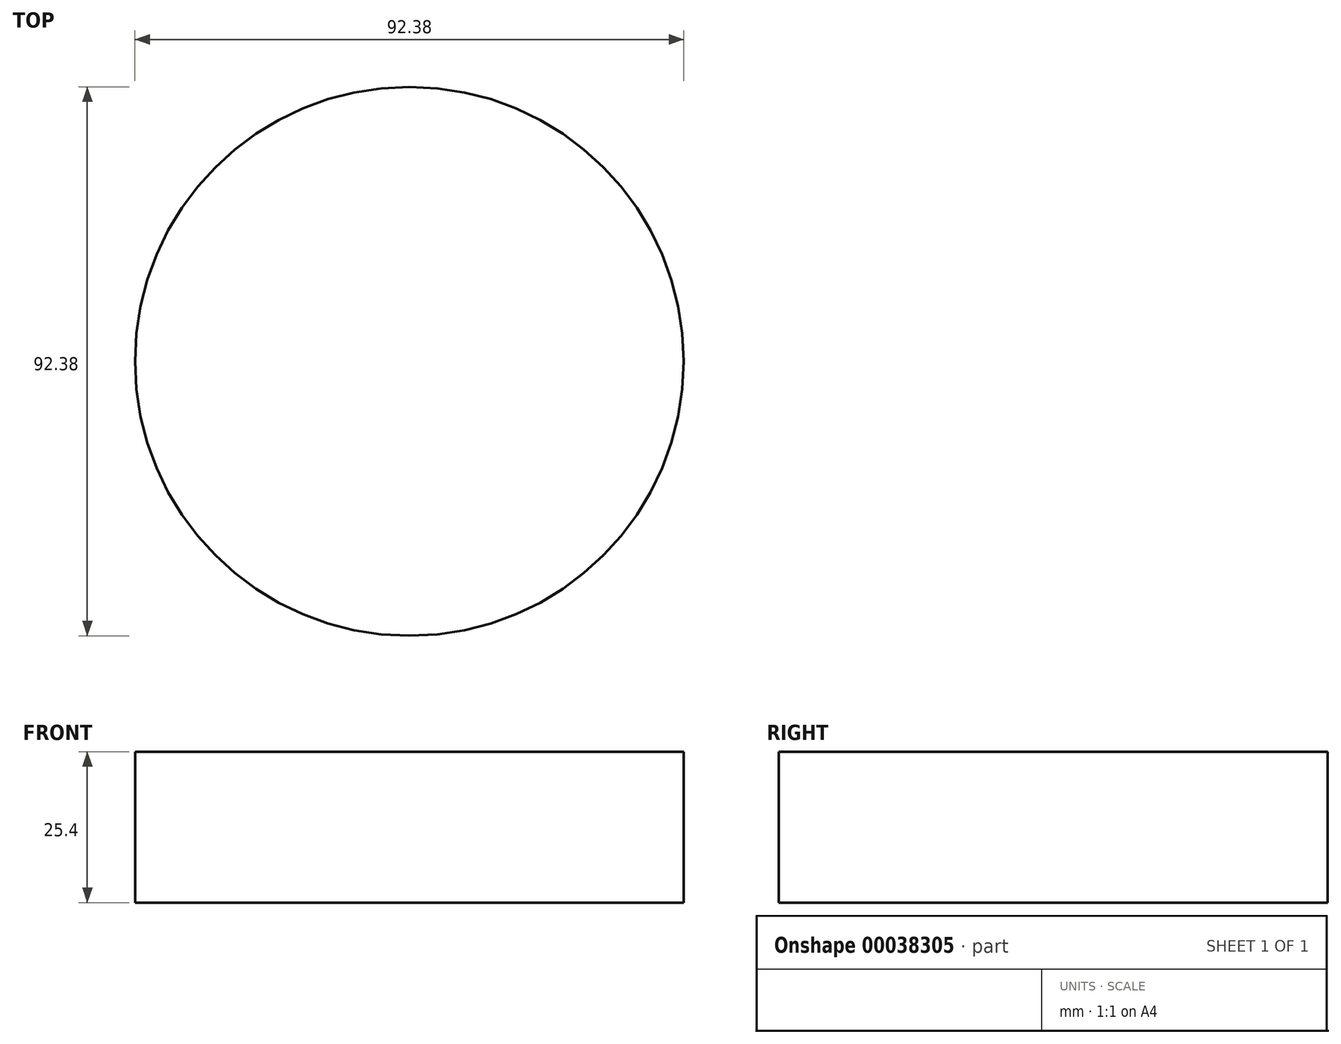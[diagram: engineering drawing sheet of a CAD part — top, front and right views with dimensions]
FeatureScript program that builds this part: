
annotation { "Feature Type Name" : "Feature", "Feature Type Description" : "" }
export const myFeature = defineFeature(function(context is Context, id is Id, definition is map)
    precondition{}
    {
        {
            var Q0;
            Q0=qCreatedBy(makeId("Top.planeOp"),FACE);
            var sketch = newSketch(context, id + "F0", { "sketchPlane" : qUnion([Q0])});
            skCircle(sketch, "E0", {"center": v(0, 0) * mm, "radius": 46.19 * mm});
            skSolve(sketch);
        }
        {
            var Q0;
            Q0=makeQuery(id+"F0.imprint","IMPRINT",FACE,{"disambiguationData":[TD([[makeQuery(id+"F0.imprint","IMPRINT",EDGE,{"derivedFrom":sQuery(id+"F0.wireOp",EDGE,"E0")}),1.0]])]});
            extrude(context, id + "F1", {"entities" : qUnion([Q0]), "depth" : 25.4 * mm});
        }
    });
